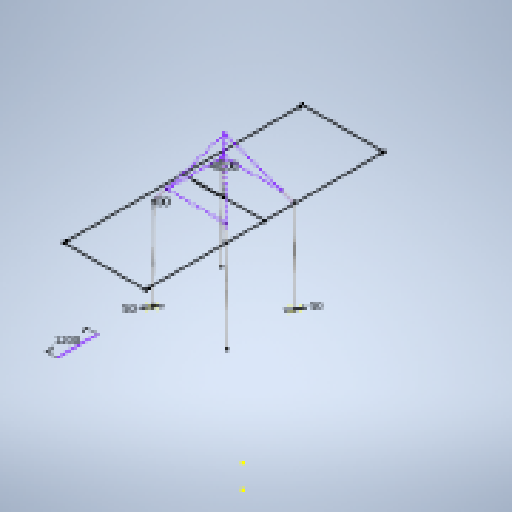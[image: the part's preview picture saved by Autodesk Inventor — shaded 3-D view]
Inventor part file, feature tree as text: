
AUTODESK INVENTOR PART (.ipt)
format: ipt  version: 2025 (Build 290162010, 162A)  size: 299,520 bytes
history: native  units: mm
features: other x8, sketch x6, sweep x4, reference x2, plane x1
ambient origin geometry x8: Origin, YZ Plane, XZ Plane, XY Plane, X Axis, Y Axis, Z Axis, Center Point
bodies: Solid1 (feature_tree)
feature tree (21):
  sketch  "3D Sketch1"
  plane  "Work Plane1"
  sweep  "Sweep1"
  sketch  "Sketch2"  dims[d2=0.0mm d3=0.0mm d4=50.0mm]
  sweep  "Sweep3"
  sweep  "Sweep5"
  sweep  "Sweep6"
  sketch  "Sketch5"  dims[d14=0.0mm d15=0.0mm d16=0.0mm d17=0.0mm d18=1200.0mm d19=1200.0mm d20=1200.0mm d21=1200.0mm d22=1200.0mm d23=6986.0mm d24=2400.0mm d25=1200.0mm d26=1200.0mm]
  sketch  "Sketch1"  dims[d0=6.981317mm d1=50.0mm]
  sketch  "Sketch3"  dims[d7=50.0mm d8=0.0mm d9=0.0mm]
  sketch  "Sketch4"  dims[d10=50.0mm d13=400.0mm]
  reference  "Reference1"
  reference  "Reference2"
  other  "<userpath>\Yandex.Disk\home pc\Inventor\PNS2-Panaevsk\ASY PNS 1200 right module.iam"
  other  "ASY PNS 1200 right module.iam"
  other  "ASY PNS 1240 frame featheredge:1"
  other  "Frame 1742035324027:1"
  other  "ISO 10799-2 100x100x4 - 2400:1"
  other  "ASY PNS 1130 frame featheredge:1"
  other  "Frame 1742042653651:1"
  other  "ISO 10799-2 100x100x3 - 2400:1"
